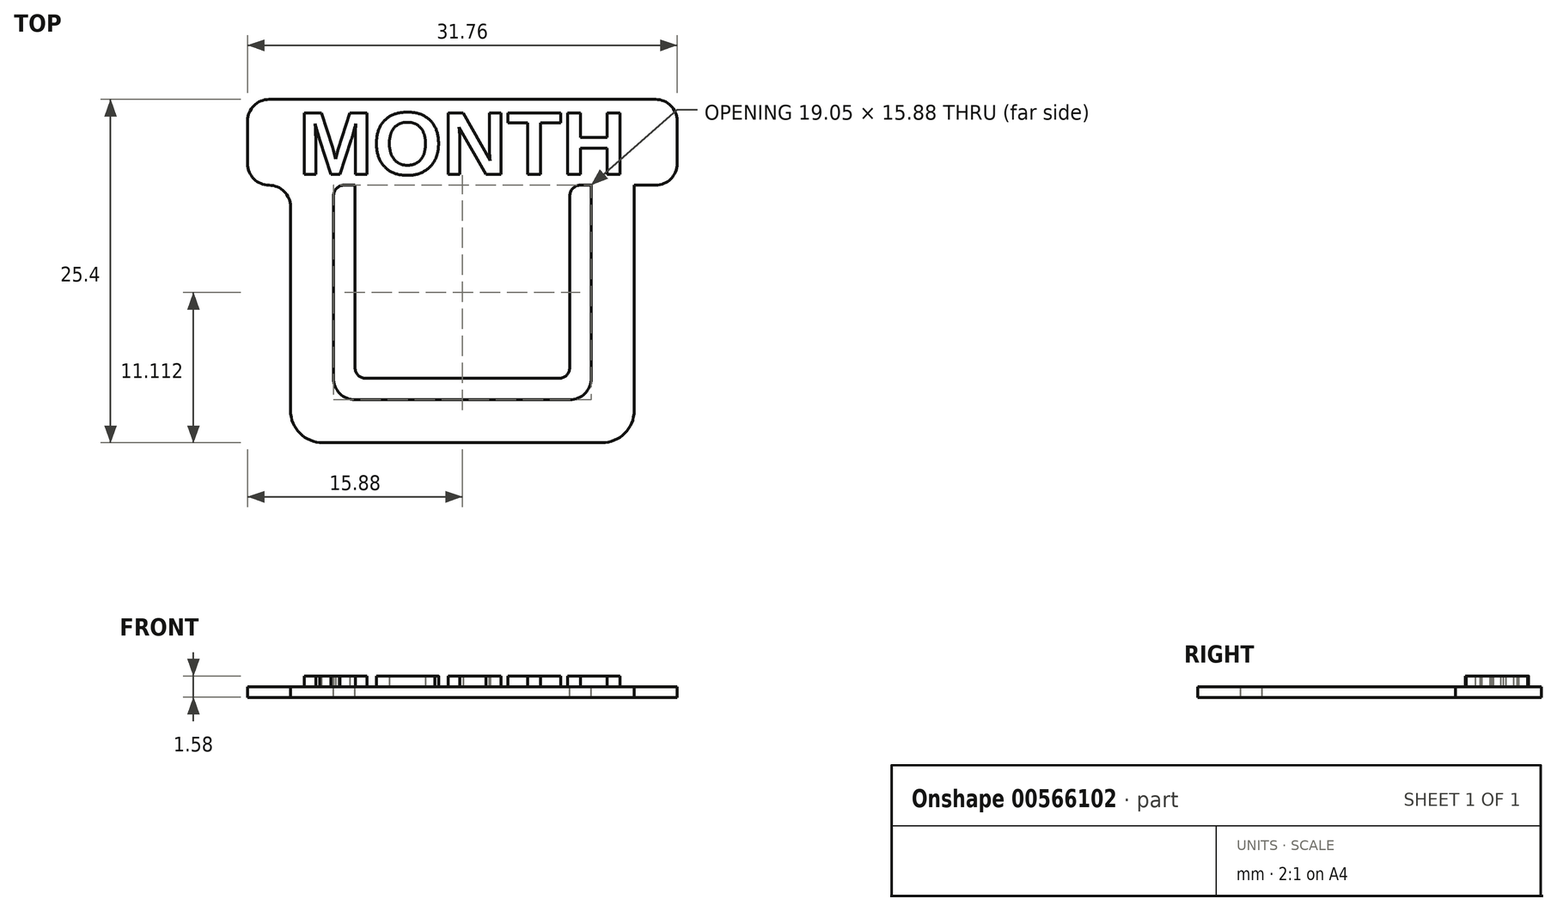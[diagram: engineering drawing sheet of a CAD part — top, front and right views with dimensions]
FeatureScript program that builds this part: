
annotation { "Feature Type Name" : "Feature", "Feature Type Description" : "" }
export const myFeature = defineFeature(function(context is Context, id is Id, definition is map)
    precondition{}
    {
        {
            var Q0;
            Q0=qCreatedBy(makeId("Front.planeOp"),FACE);
            var sketch = newSketch(context, id + "F0", { "sketchPlane" : qUnion([Q0])});
            skLineSegment(sketch, "E0.bottom", {"start": v(12.7, 9.53) * mm, "end": v(-12.7, 9.53) * mm});
            skLineSegment(sketch, "E0.top", {"start": v(12.7, -9.53) * mm, "end": v(-12.7, -9.53) * mm});
            skLineSegment(sketch, "E0.left", {"start": v(12.7, 9.53) * mm, "end": v(12.7, -9.53) * mm});
            skLineSegment(sketch, "E0.right", {"start": v(-12.7, 9.53) * mm, "end": v(-12.7, -9.53) * mm});
            skPoint(sketch, "E0.middle", {"position": v(0, 0) * mm});
            skSolve(sketch);
        }
        {
            var Q0;
            Q0=makeQuery(id+"F0.imprint","IMPRINT",FACE,{"disambiguationData":[TD([[makeQuery(id+"F0.imprint","IMPRINT",EDGE,{"derivedFrom":sQuery(id+"F0.wireOp",EDGE,"E0.bottom")}),1.0]])]});
            extrude(context, id + "F1", {"entities" : qUnion([Q0]), "depth" : 0.8 * mm, "offsetDistance" : 25.4 * mm});
        }
        {
            var Q0;
            Q0=makeQuery(id+"F1.opExtrude","SWEPT_EDGE",EDGE,{"disambiguationData":[OSD([sQuery(id+"F0.wireOp",EDGE,"E0.top"),sQuery(id+"F0.wireOp",EDGE,"E0.left")])]});
            var Q1;
            Q1=makeQuery(id+"F1.opExtrude","SWEPT_EDGE",EDGE,{"disambiguationData":[OSD([sQuery(id+"F0.wireOp",EDGE,"E0.top"),sQuery(id+"F0.wireOp",EDGE,"E0.right")])]});
            fillet(context, id + "F2", {"entities" : qUnion([Q0, Q1]), "radius" : 2.38 * mm, "tangentPropagation" : true, "allowEdgeOverflow" : false});
        }
        {
            var Q0;
            Q0=makeQuery(id+"F1.opExtrude","CAP_FACE",FACE,{"disambiguationData":[OSD([sQuery(id+"F0.wireOp",EDGE,"E0.bottom"),sQuery(id+"F0.wireOp",EDGE,"E0.top"),sQuery(id+"F0.wireOp",EDGE,"E0.left"),sQuery(id+"F0.wireOp",EDGE,"E0.right")])],"isStart":false});
            var sketch = newSketch(context, id + "F3", { "sketchPlane" : qUnion([Q0])});
            skLineSegment(sketch, "E1.bottom", {"start": v(9.52, 9.53) * mm, "end": v(-9.53, 9.53) * mm});
            skLineSegment(sketch, "E1.top", {"start": v(9.53, -6.35) * mm, "end": v(-9.53, -6.35) * mm});
            skLineSegment(sketch, "E1.left", {"start": v(9.52, 9.53) * mm, "end": v(9.53, -6.35) * mm});
            skLineSegment(sketch, "E1.right", {"start": v(-9.53, 9.53) * mm, "end": v(-9.52, -6.35) * mm});
            skPoint(sketch, "E1.middle", {"position": v(0, 0) * mm});
            skSolve(sketch);
        }
        {
            var Q0;
            Q0=makeQuery(id+"F3.imprint","IMPRINT",FACE,{"disambiguationData":[TD([[makeQuery(id+"F3.imprint","IMPRINT",EDGE,{"derivedFrom":sQuery(id+"F3.wireOp",EDGE,"E1.bottom")}),1.0]])]});
            extrude(context, id + "F4", {"entities" : qUnion([Q0]), "operationType" : NewBodyOperationType.REMOVE, "oppositeDirection" : true, "depth" : 4.93 * mm, "offsetDistance" : 25.4 * mm});
        }
        {
            var Q0;
            Q0=makeQuery(id+"F1.opExtrude","CAP_FACE",FACE,{"disambiguationData":[OSD([sQuery(id+"F0.wireOp",EDGE,"E0.bottom"),sQuery(id+"F0.wireOp",EDGE,"E0.top"),sQuery(id+"F0.wireOp",EDGE,"E0.left"),sQuery(id+"F0.wireOp",EDGE,"E0.right")])],"isStart":false});
            var sketch = newSketch(context, id + "F5", { "sketchPlane" : qUnion([Q0])});
            skLineSegment(sketch, "E2.bottom", {"start": v(-15.88, 9.53) * mm, "end": v(15.87, 9.53) * mm});
            skLineSegment(sketch, "E2.top", {"start": v(-15.88, 15.88) * mm, "end": v(15.87, 15.88) * mm});
            skLineSegment(sketch, "E2.left", {"start": v(-15.88, 9.53) * mm, "end": v(-15.88, 15.88) * mm});
            skLineSegment(sketch, "E2.right", {"start": v(15.87, 9.53) * mm, "end": v(15.87, 15.88) * mm});
            skSolve(sketch);
        }
        {
            var Q0;
            Q0=makeQuery(id+"F5.imprint","IMPRINT",FACE,{"disambiguationData":[TD([[makeQuery(id+"F5.imprint","IMPRINT",EDGE,{"derivedFrom":sQuery(id+"F5.wireOp",EDGE,"E2.top")}),-1.0]])]});
            extrude(context, id + "F6", {"entities" : qUnion([Q0]), "operationType" : NewBodyOperationType.ADD, "oppositeDirection" : true, "depth" : 0.8 * mm, "offsetDistance" : 25.4 * mm});
        }
        {
            var Q0;
            Q0=makeQuery(id+"F6.opExtrude","SWEPT_EDGE",EDGE,{"disambiguationData":[OSD([sQuery(id+"F5.wireOp",EDGE,"E2.top"),sQuery(id+"F5.wireOp",EDGE,"E2.left")])]});
            var Q1;
            Q1=makeQuery(id+"F6.opExtrude","SWEPT_EDGE",EDGE,{"disambiguationData":[OSD([sQuery(id+"F5.wireOp",EDGE,"E2.top"),sQuery(id+"F5.wireOp",EDGE,"E2.right")])]});
            var Q2;
            Q2=makeQuery(id+"F6.opExtrude","SWEPT_EDGE",EDGE,{"disambiguationData":[OSD([sQuery(id+"F5.wireOp",EDGE,"E2.bottom"),sQuery(id+"F5.wireOp",EDGE,"E2.right")])]});
            var Q3;
            Q3=makeQuery(id+"F1.opExtrude","SWEPT_EDGE",EDGE,{"disambiguationData":[OSD([sQuery(id+"F0.wireOp",EDGE,"E0.bottom"),sQuery(id+"F0.wireOp",EDGE,"E0.left")])]});
            var Q4;
            Q4=makeQuery(id+"F6.opExtrude","SWEPT_EDGE",EDGE,{"disambiguationData":[OSD([sQuery(id+"F5.wireOp",EDGE,"E2.bottom"),sQuery(id+"F5.wireOp",EDGE,"E2.left")])]});
            var Q5;
            Q5=makeQuery(id+"F1.opExtrude","SWEPT_EDGE",EDGE,{"disambiguationData":[OSD([sQuery(id+"F0.wireOp",EDGE,"E0.bottom"),sQuery(id+"F0.wireOp",EDGE,"E0.right")])]});
            fillet(context, id + "F7", {"entities" : qUnion([Q0, Q1, Q2, Q3, Q4, Q5]), "radius" : 1.59 * mm, "tangentPropagation" : true, "allowEdgeOverflow" : false});
        }
        {
            var Q0;
            Q0=makeQuery(id+"F4.boolean.opBoolean","COPY",EDGE,{"derivedFrom":makeQuery(id+"F4.opExtrude","SWEPT_EDGE",EDGE,{"disambiguationData":[OSD([sQuery(id+"F3.wireOp",EDGE,"E1.top"),sQuery(id+"F3.wireOp",EDGE,"E1.right")])]})});
            var Q1;
            Q1=makeQuery(id+"F4.boolean.opBoolean","COPY",EDGE,{"derivedFrom":makeQuery(id+"F4.opExtrude","SWEPT_EDGE",EDGE,{"disambiguationData":[OSD([sQuery(id+"F3.wireOp",EDGE,"E1.top"),sQuery(id+"F3.wireOp",EDGE,"E1.left")])]})});
            fillet(context, id + "F8", {"entities" : qUnion([Q0, Q1]), "radius" : 1.59 * mm, "tangentPropagation" : true, "allowEdgeOverflow" : false});
        }
        {
            var Q0;
            Q0=makeQuery(id+"F6.boolean.opBoolean","MERGE",FACE,{"derivedFrom":[makeQuery(id+"F1.opExtrude","CAP_FACE",FACE,{"disambiguationData":[OSD([sQuery(id+"F0.wireOp",EDGE,"E0.bottom"),sQuery(id+"F0.wireOp",EDGE,"E0.top"),sQuery(id+"F0.wireOp",EDGE,"E0.left"),sQuery(id+"F0.wireOp",EDGE,"E0.right")])],"isStart":false}),makeQuery(id+"F6.opExtrude","CAP_FACE",FACE,{"disambiguationData":[OSD([sQuery(id+"F5.wireOp",EDGE,"E2.bottom"),sQuery(id+"F5.wireOp",EDGE,"E2.top"),sQuery(id+"F5.wireOp",EDGE,"E2.left"),sQuery(id+"F5.wireOp",EDGE,"E2.right")])],"isStart":true})]});
            var sketch = newSketch(context, id + "F9", { "sketchPlane" : qUnion([Q0])});
            skLineSegment(sketch, "E3.bottom", {"start": v(-7.94, 9.53) * mm, "end": v(7.94, 9.53) * mm});
            skLineSegment(sketch, "E3.top", {"start": v(-7.94, -4.76) * mm, "end": v(7.94, -4.76) * mm});
            skLineSegment(sketch, "E3.left", {"start": v(-7.94, 9.53) * mm, "end": v(-7.94, -4.76) * mm});
            skLineSegment(sketch, "E3.right", {"start": v(7.94, 9.53) * mm, "end": v(7.94, -4.76) * mm});
            skSolve(sketch);
        }
        {
            var Q0;
            Q0=makeQuery(id+"F9.imprint","IMPRINT",FACE,{"disambiguationData":[TD([[makeQuery(id+"F9.imprint","IMPRINT",EDGE,{"derivedFrom":sQuery(id+"F9.wireOp",EDGE,"E3.bottom")}),1.0]])]});
            extrude(context, id + "F10", {"entities" : qUnion([Q0]), "operationType" : NewBodyOperationType.ADD, "oppositeDirection" : true, "depth" : 0.8 * mm, "offsetDistance" : 25.4 * mm});
        }
        {
            var Q0;
            Q0=makeQuery(id+"F10.boolean.opBoolean","MERGE",FACE,{"derivedFrom":[makeQuery(id+"F6.boolean.opBoolean","MERGE",FACE,{"derivedFrom":[makeQuery(id+"F1.opExtrude","CAP_FACE",FACE,{"disambiguationData":[OSD([sQuery(id+"F0.wireOp",EDGE,"E0.bottom"),sQuery(id+"F0.wireOp",EDGE,"E0.top"),sQuery(id+"F0.wireOp",EDGE,"E0.left"),sQuery(id+"F0.wireOp",EDGE,"E0.right")])],"isStart":false}),makeQuery(id+"F6.opExtrude","CAP_FACE",FACE,{"disambiguationData":[OSD([sQuery(id+"F5.wireOp",EDGE,"E2.bottom"),sQuery(id+"F5.wireOp",EDGE,"E2.top"),sQuery(id+"F5.wireOp",EDGE,"E2.left"),sQuery(id+"F5.wireOp",EDGE,"E2.right")])],"isStart":true})]}),makeQuery(id+"F10.opExtrude","CAP_FACE",FACE,{"disambiguationData":[OSD([sQuery(id+"F9.wireOp",EDGE,"E3.bottom"),sQuery(id+"F9.wireOp",EDGE,"E3.top"),sQuery(id+"F9.wireOp",EDGE,"E3.left"),sQuery(id+"F9.wireOp",EDGE,"E3.right")])],"isStart":true})]});
            var sketch = newSketch(context, id + "F11", { "sketchPlane" : qUnion([Q0])});
            skText(sketch, "E4", { "text": "MONTH", "fontName": "Arimo-Bold.ttf"});
            const initialGuessF11  = {"E4": [-0.01213, 0.01032, 1, 0, 0.00476]};
            skSetInitialGuess(sketch, initialGuessF11);
            skSolve(sketch);
        }
        {
            var Q0;
            Q0=makeQuery(id+"F11.imprint","IMPRINT",FACE,{"disambiguationData":[TD([[makeQuery(id+"F11.imprint","IMPRINT",EDGE,{"derivedFrom":sQuery(id+"F11.wireOp",EDGE,"E4.sketch_text.stroke-0")}),-1.0]])]});
            var Q1;
            Q1=makeQuery(id+"F11.imprint","IMPRINT",FACE,{"disambiguationData":[TD([[makeQuery(id+"F11.imprint","IMPRINT",EDGE,{"derivedFrom":sQuery(id+"F11.wireOp",EDGE,"E4.sketch_text.stroke-8")}),-1.0]])]});
            var Q2;
            Q2=makeQuery(id+"F11.imprint","IMPRINT",FACE,{"disambiguationData":[TD([[makeQuery(id+"F11.imprint","IMPRINT",EDGE,{"derivedFrom":sQuery(id+"F11.wireOp",EDGE,"E4.sketch_text.stroke-25")}),-1.0]])]});
            var Q3;
            Q3=makeQuery(id+"F11.imprint","IMPRINT",FACE,{"disambiguationData":[TD([[makeQuery(id+"F11.imprint","IMPRINT",EDGE,{"derivedFrom":sQuery(id+"F11.wireOp",EDGE,"E4.sketch_text.stroke-40")}),-1.0]])]});
            var Q4;
            Q4=makeQuery(id+"F11.imprint","IMPRINT",FACE,{"disambiguationData":[TD([[makeQuery(id+"F11.imprint","IMPRINT",EDGE,{"derivedFrom":sQuery(id+"F11.wireOp",EDGE,"E4.sketch_text.stroke-55")}),-1.0]])]});
            var Q5;
            Q5=makeQuery(id+"F11.imprint","IMPRINT",FACE,{"disambiguationData":[TD([[makeQuery(id+"F11.imprint","IMPRINT",EDGE,{"derivedFrom":sQuery(id+"F11.wireOp",EDGE,"E4.sketch_text.stroke-58")}),-1.0]])]});
            extrude(context, id + "F12", {"entities" : qUnion([Q0, Q1, Q2, Q3, Q4, Q5]), "operationType" : NewBodyOperationType.ADD, "depth" : 0.8 * mm, "offsetDistance" : 25.4 * mm});
        }
        {
            var Q0;
            Q0=makeQuery(id+"F10.opExtrude","SWEPT_EDGE",EDGE,{"disambiguationData":[OSD([sQuery(id+"F5.wireOp",EDGE,"E2.bottom"),sQuery(id+"F9.wireOp",EDGE,"E3.bottom"),sQuery(id+"F9.wireOp",EDGE,"E3.left")])]});
            var Q1;
            Q1=makeQuery(id+"F4.boolean.opBoolean","COPY",EDGE,{"derivedFrom":makeQuery(id+"F4.opExtrude","SWEPT_EDGE",EDGE,{"disambiguationData":[OSD([sQuery(id+"F0.wireOp",EDGE,"E0.bottom"),sQuery(id+"F3.wireOp",EDGE,"E1.bottom"),sQuery(id+"F3.wireOp",EDGE,"E1.right")])]})});
            var Q2;
            Q2=makeQuery(id+"F10.opExtrude","SWEPT_EDGE",EDGE,{"disambiguationData":[OSD([sQuery(id+"F5.wireOp",EDGE,"E2.bottom"),sQuery(id+"F9.wireOp",EDGE,"E3.bottom"),sQuery(id+"F9.wireOp",EDGE,"E3.right")])]});
            var Q3;
            Q3=makeQuery(id+"F4.boolean.opBoolean","COPY",EDGE,{"derivedFrom":makeQuery(id+"F4.opExtrude","SWEPT_EDGE",EDGE,{"disambiguationData":[OSD([sQuery(id+"F0.wireOp",EDGE,"E0.bottom"),sQuery(id+"F3.wireOp",EDGE,"E1.bottom"),sQuery(id+"F3.wireOp",EDGE,"E1.left")])]})});
            fillet(context, id + "F13", {"entities" : qUnion([Q0, Q1, Q2, Q3]), "radius" : 0.8 * mm, "tangentPropagation" : true, "allowEdgeOverflow" : false});
        }
        {
            var Q0;
            Q0=makeQuery(id+"F10.opExtrude","SWEPT_EDGE",EDGE,{"disambiguationData":[OSD([sQuery(id+"F9.wireOp",EDGE,"E3.top"),sQuery(id+"F9.wireOp",EDGE,"E3.left")])]});
            var Q1;
            Q1=makeQuery(id+"F10.opExtrude","SWEPT_EDGE",EDGE,{"disambiguationData":[OSD([sQuery(id+"F9.wireOp",EDGE,"E3.top"),sQuery(id+"F9.wireOp",EDGE,"E3.right")])]});
            fillet(context, id + "F14", {"entities" : qUnion([Q0, Q1]), "radius" : 0.8 * mm, "tangentPropagation" : true, "allowEdgeOverflow" : false});
        }
        {
            var Q0;
            Q0=makeQuery(id+"F1.opExtrude","SWEPT_BODY",BODY,{"disambiguationData":[OSD([sQuery(id+"F0.wireOp",EDGE,"E0.bottom"),sQuery(id+"F0.wireOp",EDGE,"E0.top"),sQuery(id+"F0.wireOp",EDGE,"E0.left"),sQuery(id+"F0.wireOp",EDGE,"E0.right")])]});
            var Q1;
            Q1=makeQuery(id+"F6.opExtrude","CAP_EDGE",EDGE,{"disambiguationData":[OSD([sQuery(id+"F5.wireOp",EDGE,"E2.top")])],"isStart":false});
            transform(context, id + "F15", {"entities" : qUnion([Q0]), "transformType" : TransformType.ROTATION, "transformAxis" : qUnion([Q1]), "angle" : 270 * degree, "makeCopy" : false});
        }
    });
